# Revit family: BIMLIB_Термостатический_клапан_TGD_РОСТерм
name_source: partatom
category: Арматура трубопроводов
revit_build: Autodesk Revit 2017 (Build: 20170118_1100(x64)
units: mm (PartAtom-declared; Revit-internal decimal feet)

## family parameters
Всегда вертикально = Нет
На основе рабочей плоскости = Нет
Общий = Нет
При загрузке вырезать с полостями = Нет
Размер круглого соединителя = Использовать диаметр
Тип детали = Клапан - Вставляется

## types (1)
- HEIZEN TGD
    ADSK_URL документации изделия = http://rostherm.ru
    ADSK_URL страницы изделия = http://rostherm.ru
    ADSK_Версия Revit = 2017
    ADSK_Единица измерения = шт.
    ADSK_Завод-изготовитель = Heizen
    ADSK_Масса = 0
    ADSK_Материал = BIMLIB_Латунь_РТ
    BL_BIM library = https://bimlib.pro
    URL = http://rostherm.ru
    Изготовитель = РОСТерм
    Коэффициент K = 0
    Метод определения потерь = Не задано
    Описание = Термостатический радиаторный клапан с повышенной пропускной способностью для однотрубных гравитационных систем отопления или систем с высоким значением расхода. Возможно исполнение в прямом и угловом вариантах. Подходит для всех термостатических элементов Heizen, кроме элементов 3 серии с клипсовым соединением
    РТ_Номинальное давление = 10.0 бары

## geometry (parser evidence)
native form markers: Sweep x6
no freeform markers — native parametric forms only
